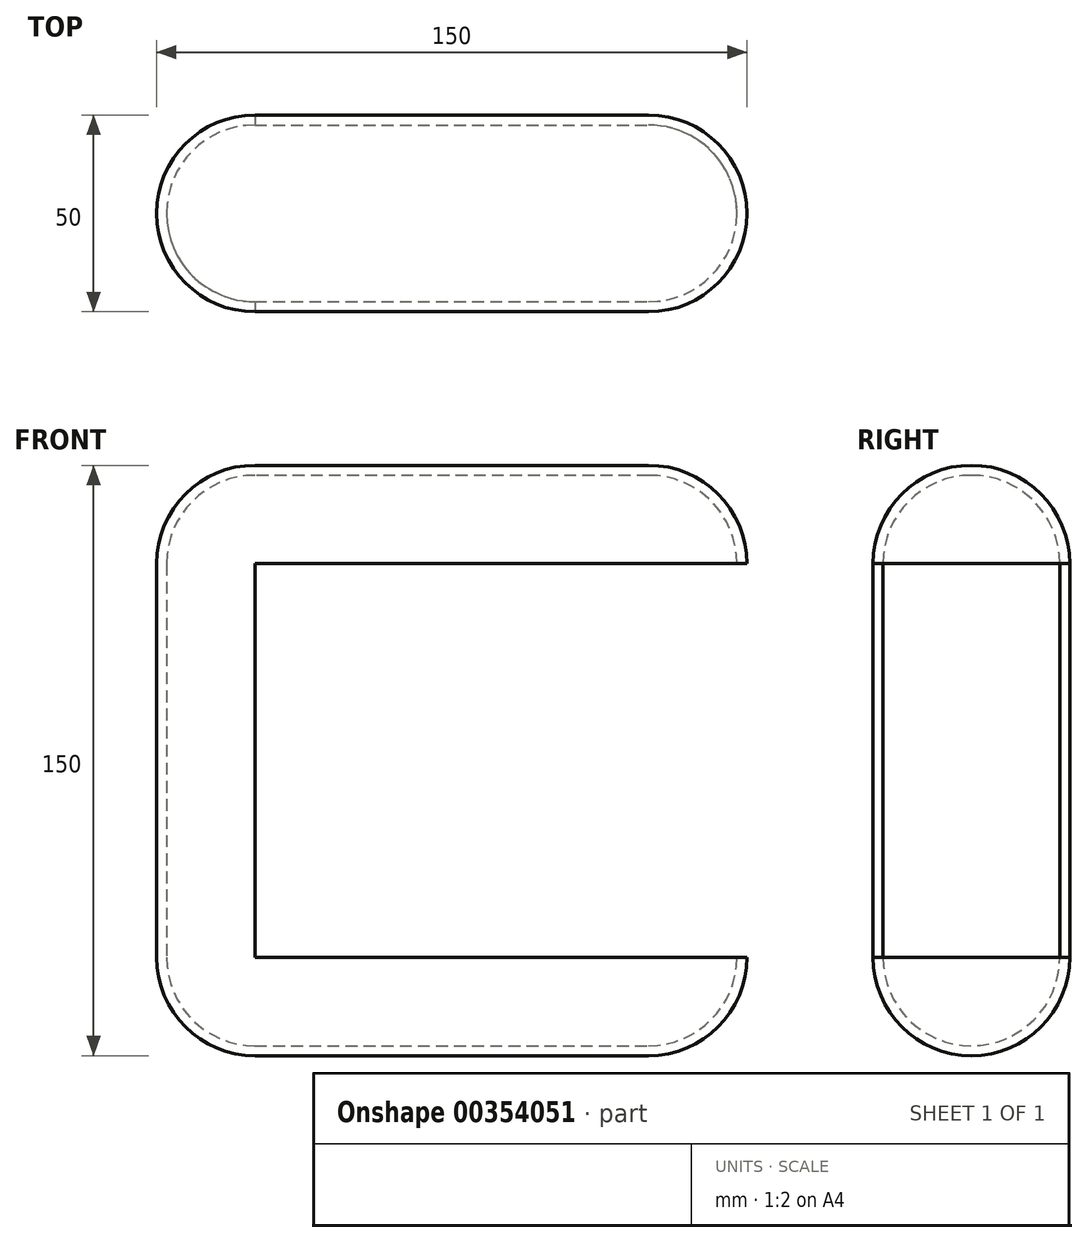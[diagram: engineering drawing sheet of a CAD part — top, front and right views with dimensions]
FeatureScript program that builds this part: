
annotation { "Feature Type Name" : "Feature", "Feature Type Description" : "" }
export const myFeature = defineFeature(function(context is Context, id is Id, definition is map)
    precondition{}
    {
        {
            var Q0;
            Q0=qCreatedBy(makeId("Front.planeOp"),FACE);
            var sketch = newSketch(context, id + "F0", { "sketchPlane" : qUnion([Q0])});
            skLineSegment(sketch, "E0.bottom", {"start": v(75, 75) * mm, "end": v(-75, 75) * mm});
            skLineSegment(sketch, "E0.top", {"start": v(75, -75) * mm, "end": v(-75, -75) * mm});
            skLineSegment(sketch, "E0.left", {"start": v(75, 75) * mm, "end": v(75, -75) * mm});
            skLineSegment(sketch, "E0.right", {"start": v(-75, 75) * mm, "end": v(-75, -75) * mm});
            skPoint(sketch, "E0.middle", {"position": v(0, 0) * mm});
            skSolve(sketch);
        }
        {
            var Q0;
            Q0=makeQuery(id+"F0.imprint","IMPRINT",FACE,{"disambiguationData":[TD([[makeQuery(id+"F0.imprint","IMPRINT",EDGE,{"derivedFrom":sQuery(id+"F0.wireOp",EDGE,"E0.bottom")}),1.0]])]});
            extrude(context, id + "F1", {"entities" : qUnion([Q0]), "depth" : 50 * mm});
        }
        {
            var Q0;
            Q0=makeQuery(id+"F1.opExtrude","SWEPT_FACE",FACE,{"disambiguationData":[OSD([sQuery(id+"F0.wireOp",EDGE,"E0.bottom")])]});
            var Q1;
            Q1=makeQuery(id+"F1.opExtrude","SWEPT_FACE",FACE,{"disambiguationData":[OSD([sQuery(id+"F0.wireOp",EDGE,"E0.right")])]});
            var Q2;
            Q2=makeQuery(id+"F1.opExtrude","SWEPT_FACE",FACE,{"disambiguationData":[OSD([sQuery(id+"F0.wireOp",EDGE,"E0.left")])]});
            var Q3;
            Q3=makeQuery(id+"F1.opExtrude","SWEPT_FACE",FACE,{"disambiguationData":[OSD([sQuery(id+"F0.wireOp",EDGE,"E0.top")])]});
            fillet(context, id + "F2", {"entities" : qUnion([Q0, Q1, Q2, Q3]), "radius" : 25 * mm, "tangentPropagation" : true, "allowEdgeOverflow" : false});
        }
        {
            var Q0;
            Q0=makeQuery(id+"F2.opFillet","BLEND_FACE",FACE,{"disambiguationData":[OSD([sQuery(id+"F0.wireOp",EDGE,"E0.left")])]});
            shell(context, id + "F3", {"entities" : qUnion([Q0]), "thickness" : 2.54 * mm});
        }
        {
            var Q0;
            Q0=makeQuery(id+"F1.opExtrude","CAP_FACE",FACE,{"disambiguationData":[OSD([sQuery(id+"F0.wireOp",EDGE,"E0.bottom"),sQuery(id+"F0.wireOp",EDGE,"E0.top"),sQuery(id+"F0.wireOp",EDGE,"E0.left"),sQuery(id+"F0.wireOp",EDGE,"E0.right")])],"isStart":false});
            extrude(context, id + "F4", {"entities" : qUnion([Q0]), "operationType" : NewBodyOperationType.REMOVE, "oppositeDirection" : true, "depth" : 25.4 * mm});
        }
        {
            var Q0;
            {var subQ0=sQuery(id+"F0.wireOp",EDGE,"E0.right");var subQ1=sQuery(id+"F0.wireOp",EDGE,"E0.left");var subQ2=sQuery(id+"F0.wireOp",EDGE,"E0.top");var subQ3=sQuery(id+"F0.wireOp",EDGE,"E0.bottom");Q0=makeQuery(id+"F3.opShell","OFFSET_FACE",FACE,{"disambiguationData":[OSD([subQ3,subQ2,subQ1,subQ0]),TDD([makeQuery(id+"F1.opExtrude","CAP_FACE",FACE,{"disambiguationData":[OSD([subQ3,subQ2,subQ1,subQ0])],"isStart":true})])]});}
            extrude(context, id + "F5", {"entities" : qUnion([Q0]), "operationType" : NewBodyOperationType.REMOVE, "oppositeDirection" : true, "depth" : 25.4 * mm});
        }
    });
